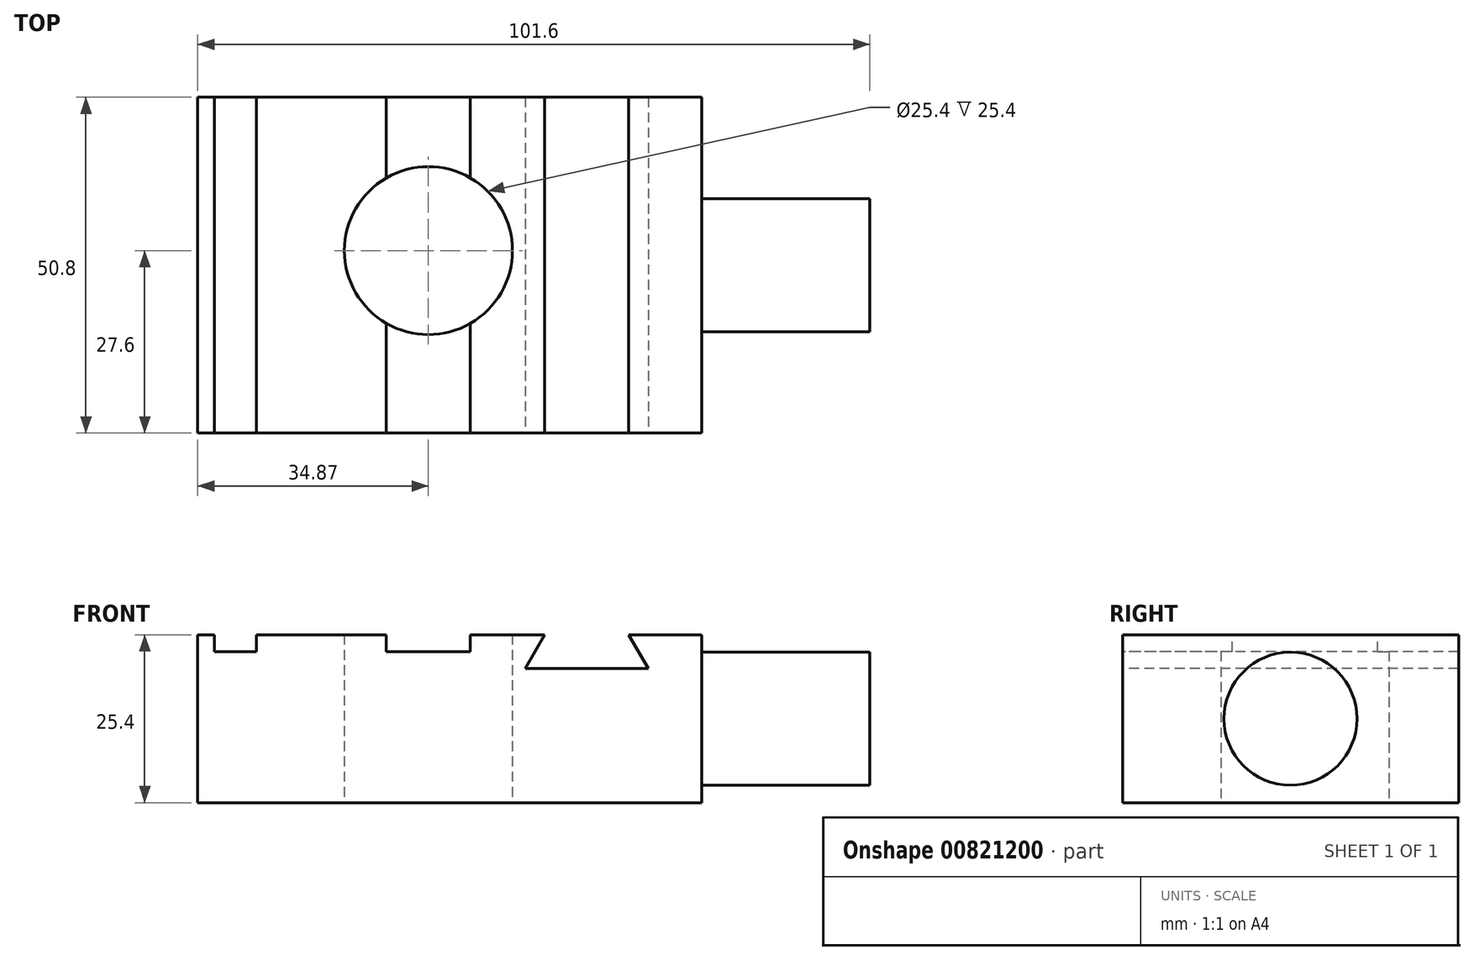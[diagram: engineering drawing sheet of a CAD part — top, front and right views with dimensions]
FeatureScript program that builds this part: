
annotation { "Feature Type Name" : "Feature", "Feature Type Description" : "" }
export const myFeature = defineFeature(function(context is Context, id is Id, definition is map)
    precondition{}
    {
        {
            var Q0;
            Q0=qCreatedBy(makeId("Top.planeOp"),FACE);
            var sketch = newSketch(context, id + "F0", { "sketchPlane" : qUnion([Q0])});
            skLineSegment(sketch, "E0.bottom", {"start": v(-34.87, 23.2) * mm, "end": v(41.33, 23.2) * mm});
            skLineSegment(sketch, "E0.top", {"start": v(-34.87, -27.6) * mm, "end": v(41.33, -27.6) * mm});
            skLineSegment(sketch, "E0.left", {"start": v(-34.87, 23.2) * mm, "end": v(-34.87, -27.6) * mm});
            skLineSegment(sketch, "E0.right", {"start": v(41.33, 23.2) * mm, "end": v(41.33, -27.6) * mm});
            skCircle(sketch, "E1", {"center": v(0, 0) * mm, "radius": 12.7 * mm});
            skSolve(sketch);
        }
        {
            var Q0;
            Q0=makeQuery(id+"F0.imprint","IMPRINT",FACE,{"disambiguationData":[TD([[makeQuery(id+"F0.imprint","IMPRINT",EDGE,{"derivedFrom":sQuery(id+"F0.wireOp",EDGE,"E0.bottom")}),-1.0]])]});
            extrude(context, id + "F1", {"entities" : qUnion([Q0]), "depth" : 25.4 * mm, "offsetDistance" : 25.4 * mm});
        }
        {
            var Q0;
            Q0=makeQuery(id+"F1.opExtrude","CAP_FACE",FACE,{"disambiguationData":[OSD([sQuery(id+"F0.wireOp",EDGE,"E0.bottom"),sQuery(id+"F0.wireOp",EDGE,"E0.top"),sQuery(id+"F0.wireOp",EDGE,"E0.left"),sQuery(id+"F0.wireOp",EDGE,"E0.right"),sQuery(id+"F0.wireOp",EDGE,"E1")])],"isStart":false});
            var sketch = newSketch(context, id + "F2", { "sketchPlane" : qUnion([Q0])});
            skLineSegment(sketch, "E2.bottom", {"start": v(-32.33, 23.2) * mm, "end": v(-25.98, 23.2) * mm});
            skLineSegment(sketch, "E2.top", {"start": v(-32.33, -27.6) * mm, "end": v(-25.98, -27.6) * mm});
            skLineSegment(sketch, "E2.left", {"start": v(-32.33, 23.2) * mm, "end": v(-32.33, -27.6) * mm});
            skLineSegment(sketch, "E2.right", {"start": v(-25.98, 23.2) * mm, "end": v(-25.98, -27.6) * mm});
            skLineSegment(sketch, "E3", {"start": v(-6.35, 23.2) * mm, "end": v(-6.35, -27.6) * mm});
            skLineSegment(sketch, "E4", {"start": v(-6.35, -27.6) * mm, "end": v(6.35, -27.6) * mm});
            skLineSegment(sketch, "E5", {"start": v(6.35, -27.6) * mm, "end": v(6.35, 23.2) * mm});
            skLineSegment(sketch, "E6", {"start": v(6.35, 23.2) * mm, "end": v(-6.35, 23.2) * mm});
            skPoint(sketch, "E7", {"position": v(0, -1.82) * mm});
            skLineSegment(sketch, "E8", {"start": v(0, 23.2) * mm, "end": v(0, -27.6) * mm, "construction": true});
            skSolve(sketch);
        }
        {
            var Q0;
            Q0=makeQuery(id+"F2.imprint","IMPRINT",FACE,{"disambiguationData":[TD([[makeQuery(id+"F2.imprint","IMPRINT",EDGE,{"derivedFrom":sQuery(id+"F2.wireOp",EDGE,"E2.bottom")}),-1.0]])]});
            var Q1;
            {var subQ0=sQuery(id+"F2.wireOp",EDGE,"E4");Q1=makeQuery(id+"F2.imprint","IMPRINT",FACE,{"disambiguationData":[TD([[makeQuery(id+"F2.imprint","IMPRINT",EDGE,{"derivedFrom":subQ0}),1.0]])]});}
            var Q2;
            {var subQ0=sQuery(id+"F2.wireOp",EDGE,"E6");Q2=makeQuery(id+"F2.imprint","IMPRINT",FACE,{"disambiguationData":[TD([[makeQuery(id+"F2.imprint","IMPRINT",EDGE,{"derivedFrom":subQ0}),-1.0]])]});}
            extrude(context, id + "F3", {"entities" : qUnion([Q0, Q1, Q2]), "operationType" : NewBodyOperationType.REMOVE, "oppositeDirection" : true, "depth" : 2.54 * mm, "offsetDistance" : 25.4 * mm});
        }
        {
            var Q0;
            Q0=makeQuery(id+"F1.opExtrude","SWEPT_FACE",FACE,{"disambiguationData":[OSD([sQuery(id+"F0.wireOp",EDGE,"E0.top")])]});
            var sketch = newSketch(context, id + "F4", { "sketchPlane" : qUnion([Q0])});
            skLineSegment(sketch, "E9", {"start": v(17.59, 25.4) * mm, "end": v(14.65, 20.32) * mm});
            skLineSegment(sketch, "E10", {"start": v(14.65, 20.32) * mm, "end": v(33.22, 20.32) * mm});
            skLineSegment(sketch, "E11", {"start": v(33.22, 20.32) * mm, "end": v(30.29, 25.4) * mm});
            skLineSegment(sketch, "E12", {"start": v(30.29, 25.4) * mm, "end": v(17.59, 25.4) * mm});
            skSolve(sketch);
        }
        {
            var Q0;
            Q0=makeQuery(id+"F1.opExtrude","SWEPT_FACE",FACE,{"disambiguationData":[OSD([sQuery(id+"F0.wireOp",EDGE,"E0.right")])]});
            var sketch = newSketch(context, id + "F5", { "sketchPlane" : qUnion([Q0])});
            skCircle(sketch, "E13", {"center": v(-2.2, 12.7) * mm, "radius": 10.06 * mm});
            skPoint(sketch, "E13.centerSnap0", {"position": v(-2.2, 25.4) * mm});
            skPoint(sketch, "E13.centerSnap1", {"position": v(-27.6, 12.7) * mm});
            skSolve(sketch);
        }
        {
            var Q0;
            Q0=qSketchRegion(id+"F5",true);
            extrude(context, id + "F6", {"entities" : qUnion([Q0]), "operationType" : NewBodyOperationType.ADD, "depth" : 25.4 * mm, "offsetDistance" : 25.4 * mm});
        }
        {
            var Q0;
            Q0=qSketchRegion(id+"F5",true);
            extrude(context, id + "F7", {"entities" : qUnion([Q0]), "operationType" : NewBodyOperationType.ADD, "oppositeDirection" : true, "depth" : 12.45 * mm, "offsetDistance" : 25.4 * mm});
        }
        {
            var Q0;
            Q0=makeQuery(id+"F4.imprint","IMPRINT",FACE,{"disambiguationData":[TD([[makeQuery(id+"F4.imprint","IMPRINT",EDGE,{"derivedFrom":sQuery(id+"F4.wireOp",EDGE,"E9")}),1.0]])]});
            extrude(context, id + "F8", {"entities" : qUnion([Q0]), "operationType" : NewBodyOperationType.REMOVE, "oppositeDirection" : true, "depth" : 70.36 * mm, "offsetDistance" : 25.4 * mm});
        }
    });
